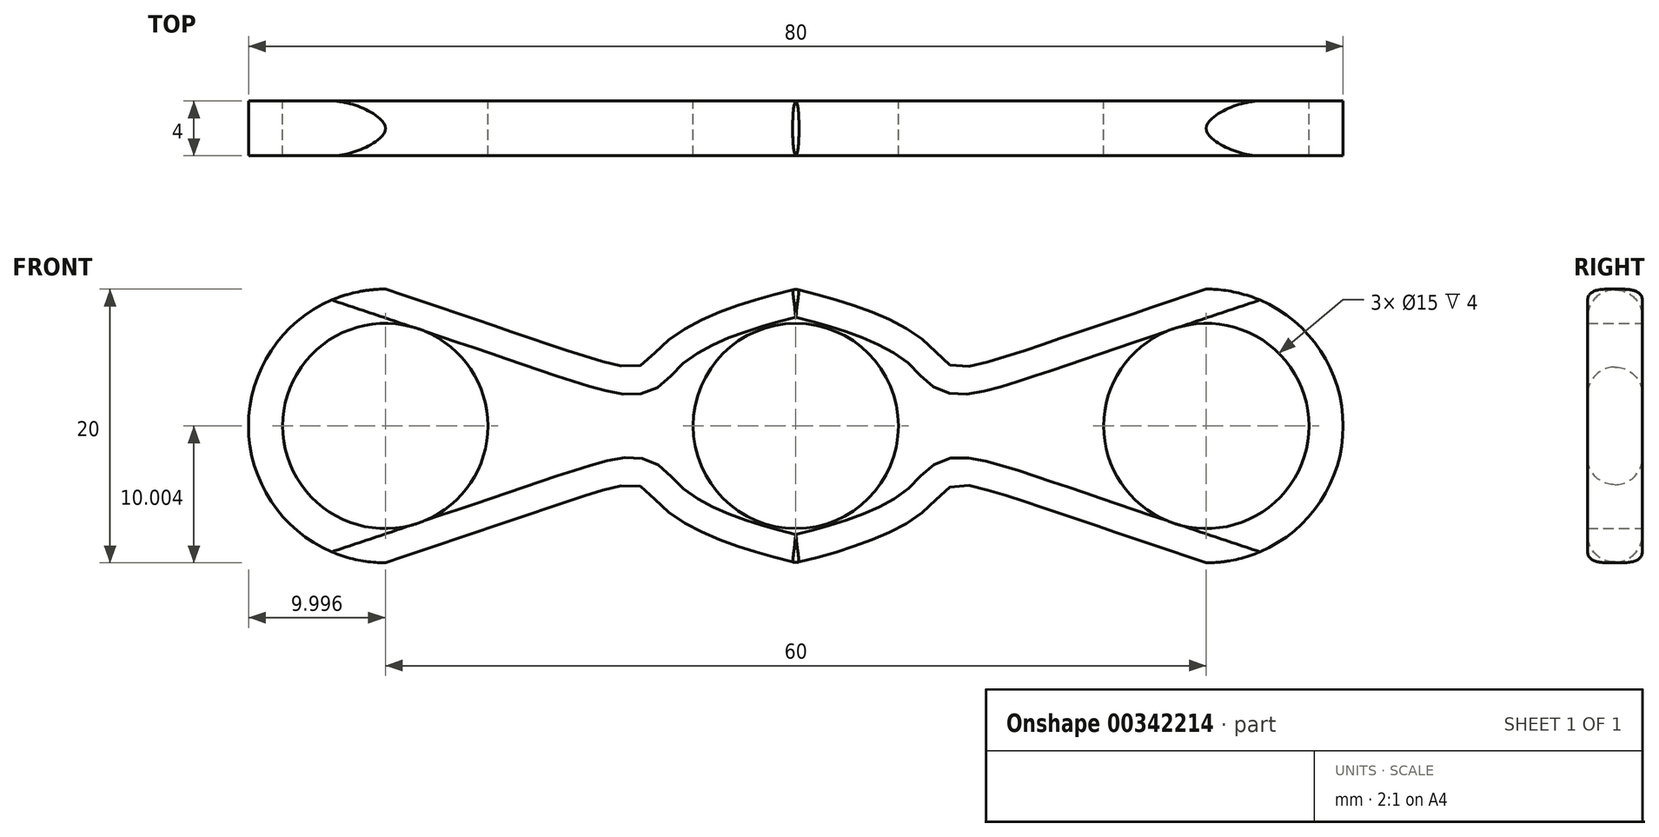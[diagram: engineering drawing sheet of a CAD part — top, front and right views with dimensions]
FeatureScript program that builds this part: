
annotation { "Feature Type Name" : "Feature", "Feature Type Description" : "" }
export const myFeature = defineFeature(function(context is Context, id is Id, definition is map)
    precondition{}
    {
        {
            var Q0;
            Q0=qCreatedBy(makeId("Front.planeOp"),FACE);
            var sketch = newSketch(context, id + "F0", { "sketchPlane" : qUnion([Q0])});
            skLineSegment(sketch, "E0.left", {"start": v(-32.53, 13.05) * mm, "end": v(-32.53, 13.05) * mm});
            skLineSegment(sketch, "E0.right", {"start": v(47.47, 13.05) * mm, "end": v(47.47, 13.05) * mm});
            skLineSegment(sketch, "E1", {"start": v(7.47, 23.05) * mm, "end": v(7.47, 3.05) * mm, "construction": true});
            skCircle(sketch, "E2", {"center": v(7.47, 13.05) * mm, "radius": 7.5 * mm});
            skLineSegment(sketch, "E3", {"start": v(27.47, 23.05) * mm, "end": v(27.47, 3.05) * mm, "construction": true});
            skLineSegment(sketch, "E4.MirrorCS", {"start": v(-12.53, 23.05) * mm, "end": v(-12.53, 3.05) * mm, "construction": true});
            skLineSegment(sketch, "E5", {"start": v(-32.53, 13.05) * mm, "end": v(47.47, 13.05) * mm, "construction": true});
            skCircle(sketch, "E6", {"center": v(37.47, 13.05) * mm, "radius": 7.5 * mm});
            skCircle(sketch, "E7.MirrorC", {"center": v(-22.53, 13.05) * mm, "radius": 7.5 * mm});
            skPoint(sketch, "E8.visualSharp", {"position": v(-32.53, 23.05) * mm});
            skArc(sketch, "E8.filletArc", {"start": v(-22.53, 23.05) * mm, "mid": v(-29.6, 20.13) * mm, "end": v(-32.53, 13.05) * mm});
            skPoint(sketch, "E9.visualSharp", {"position": v(-32.53, 3.05) * mm});
            skArc(sketch, "E9.filletArc", {"start": v(-32.53, 13.05) * mm, "mid": v(-29.6, 5.98) * mm, "end": v(-22.53, 3.05) * mm});
            skPoint(sketch, "E10.visualSharp", {"position": v(47.47, 23.05) * mm});
            skArc(sketch, "E10.filletArc", {"start": v(47.47, 13.05) * mm, "mid": v(44.54, 20.13) * mm, "end": v(37.47, 23.05) * mm});
            skPoint(sketch, "E11.visualSharp", {"position": v(47.47, 3.05) * mm});
            skArc(sketch, "E11.filletArc", {"start": v(37.47, 3.05) * mm, "mid": v(44.54, 5.98) * mm, "end": v(47.47, 13.05) * mm});
            skFitSpline(sketch, "E12", {"points": [v(-22.53, 23.05) * mm, v(7.47, 23.05) * mm], "startDerivative": vector(90, -30) * mm, "endDerivative": vector(60, 14.29) * mm});
            skFitSpline(sketch, "E13.MirrorCS", {"points": [v(37.47, 23.05) * mm, v(7.47, 23.05) * mm], "startDerivative": vector(-90, -30) * mm, "endDerivative": vector(-60, 14.29) * mm});
            skFitSpline(sketch, "E14.MirrorCS", {"points": [v(-22.53, 3.05) * mm, v(7.47, 3.05) * mm], "startDerivative": vector(90, 30) * mm, "endDerivative": vector(60, -14.29) * mm});
            skFitSpline(sketch, "E15.MirrorCS", {"points": [v(37.47, 3.05) * mm, v(7.47, 3.05) * mm], "startDerivative": vector(-90, 30) * mm, "endDerivative": vector(-60, -14.29) * mm});
            skSolve(sketch);
        }
        {
            var Q0;
            Q0=makeQuery(id+"F0.imprint","IMPRINT",FACE,{"disambiguationData":[TD([[makeQuery(id+"F0.imprint","IMPRINT",EDGE,{"derivedFrom":sQuery(id+"F0.wireOp",EDGE,"E2")}),-1.0]])]});
            extrude(context, id + "F1", {"entities" : qUnion([Q0]), "depth" : 4 * mm});
        }
        {
            var Q0;
            Q0=makeQuery(id+"F1.opExtrude","CAP_EDGE",EDGE,{"disambiguationData":[OSD([sQuery(id+"F0.wireOp",EDGE,"E12")])],"isStart":false});
            var Q1;
            Q1=makeQuery(id+"F1.opExtrude","CAP_EDGE",EDGE,{"disambiguationData":[OSD([sQuery(id+"F0.wireOp",EDGE,"E13.MirrorCS")])],"isStart":false});
            var Q2;
            Q2=makeQuery(id+"F1.opExtrude","CAP_EDGE",EDGE,{"disambiguationData":[OSD([sQuery(id+"F0.wireOp",EDGE,"E15.MirrorCS")])],"isStart":true});
            var Q3;
            Q3=makeQuery(id+"F1.opExtrude","CAP_EDGE",EDGE,{"disambiguationData":[OSD([sQuery(id+"F0.wireOp",EDGE,"E14.MirrorCS")])],"isStart":true});
            var Q4;
            Q4=makeQuery(id+"F1.opExtrude","CAP_EDGE",EDGE,{"disambiguationData":[OSD([sQuery(id+"F0.wireOp",EDGE,"E12")])],"isStart":true});
            var Q5;
            Q5=makeQuery(id+"F1.opExtrude","CAP_EDGE",EDGE,{"disambiguationData":[OSD([sQuery(id+"F0.wireOp",EDGE,"E13.MirrorCS")])],"isStart":true});
            var Q6;
            Q6=makeQuery(id+"F1.opExtrude","CAP_EDGE",EDGE,{"disambiguationData":[OSD([sQuery(id+"F0.wireOp",EDGE,"E15.MirrorCS")])],"isStart":false});
            var Q7;
            Q7=makeQuery(id+"F1.opExtrude","CAP_EDGE",EDGE,{"disambiguationData":[OSD([sQuery(id+"F0.wireOp",EDGE,"E14.MirrorCS")])],"isStart":false});
            fillet(context, id + "F2", {"entities" : qUnion([Q0, Q1, Q2, Q3, Q4, Q5, Q6, Q7]), "radius" : 2 * mm, "tangentPropagation" : true, "allowEdgeOverflow" : false});
        }
        {
            var Q0;
            Q0=makeQuery(id+"F2.opFillet","BLEND_EDGE",EDGE,{"blendedFrom":[makeQuery(id+"F1.opExtrude","CAP_EDGE",EDGE,{"disambiguationData":[OSD([sQuery(id+"F0.wireOp",EDGE,"E12")])],"isStart":false}),makeQuery(id+"F1.opExtrude","CAP_EDGE",EDGE,{"disambiguationData":[OSD([sQuery(id+"F0.wireOp",EDGE,"E13.MirrorCS")])],"isStart":false})],"blendedInto":[]});
            var Q1;
            Q1=makeQuery(id+"F2.opFillet","BLEND_EDGE",EDGE,{"blendedFrom":[makeQuery(id+"F1.opExtrude","CAP_EDGE",EDGE,{"disambiguationData":[OSD([sQuery(id+"F0.wireOp",EDGE,"E12")])],"isStart":true}),makeQuery(id+"F1.opExtrude","CAP_EDGE",EDGE,{"disambiguationData":[OSD([sQuery(id+"F0.wireOp",EDGE,"E13.MirrorCS")])],"isStart":true})],"blendedInto":[]});
            var Q2;
            Q2=makeQuery(id+"F2.opFillet","BLEND_EDGE",EDGE,{"blendedFrom":[makeQuery(id+"F1.opExtrude","CAP_EDGE",EDGE,{"disambiguationData":[OSD([sQuery(id+"F0.wireOp",EDGE,"E14.MirrorCS")])],"isStart":false}),makeQuery(id+"F1.opExtrude","CAP_EDGE",EDGE,{"disambiguationData":[OSD([sQuery(id+"F0.wireOp",EDGE,"E15.MirrorCS")])],"isStart":false})],"blendedInto":[]});
            fillet(context, id + "F3", {"entities" : qUnion([Q0, Q1, Q2]), "radius" : 1 * mm, "tangentPropagation" : true, "allowEdgeOverflow" : false});
        }
    });
